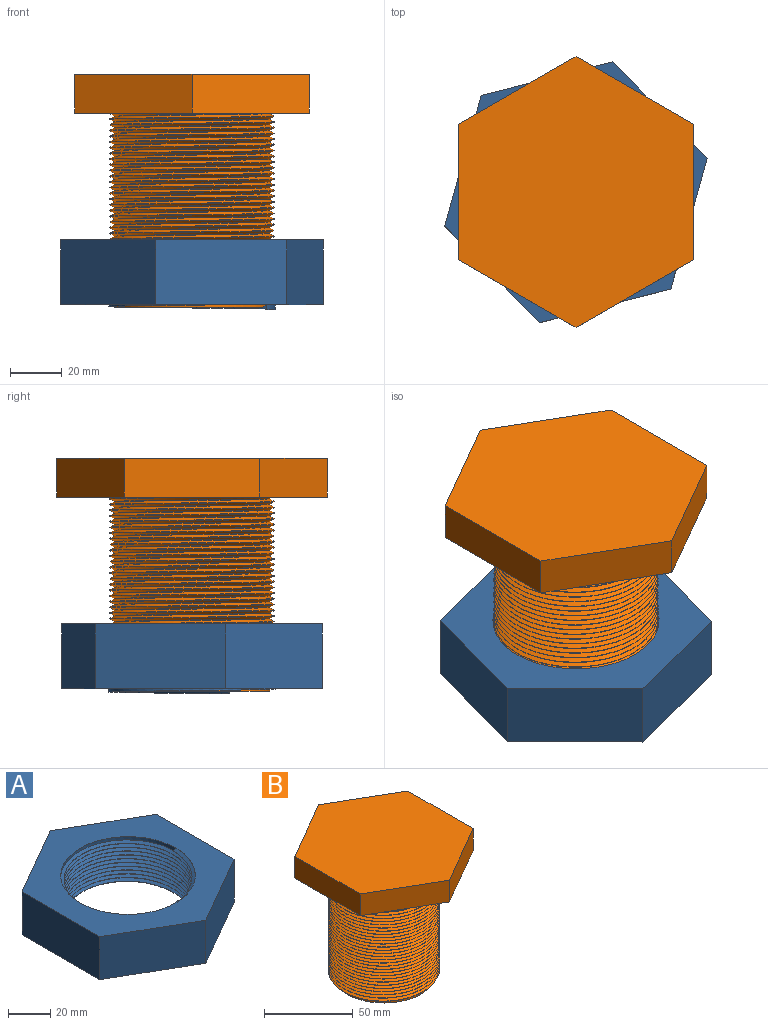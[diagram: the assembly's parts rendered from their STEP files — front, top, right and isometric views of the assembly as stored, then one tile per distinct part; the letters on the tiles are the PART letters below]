
ASSEMBLY  parts=2 mates=1
PART A: 16 faces, bbox 90.3x104.3x27.3 mm
  f0: cylinder r=32mm len=64mm, axis (0,0,-1), area 1153.5mm2, adj f1,f8,f9,f10,f12,f14
  f1: plane 104.31x90.34mm, normal (0,0,1), area 3849.1mm2, adj f0,f2,f3,f4,f5,f6,f7,f9
  f2: plane 52.15x25mm, normal (1,0,0), area 1303.8mm2, adj f1,f3,f7,f8
  f3: plane 45.16x26.08mm, normal (0.5,-0.87,0), area 1303.8mm2, adj f1,f2,f4,f8
  f4: plane 45.16x26.08mm, normal (-0.5,-0.87,0), area 1303.8mm2, adj f1,f3,f5,f8
  f5: plane 52.15x25mm, normal (-1,0,0), area 1303.8mm2, adj f1,f4,f6,f8
  f6: plane 45.16x26.08mm, normal (-0.5,0.87,0), area 1303.8mm2, adj f1,f5,f7,f8
  f7: plane 45.16x26.08mm, normal (0.5,0.87,0), area 1303.8mm2, adj f1,f2,f6,f8
  f8: plane 104.31x90.34mm, normal (0,0,-1), area 3841.2mm2, adj f0,f2,f3,f4,f5,f6,f7,f10
  f9: plane 1.97x1.6mm, normal (0,1,0), area 1.6mm2, adj f0,f1,f11,f12,f14,f15
  f10: plane 1.98x1.22mm, normal (-0.76,0.65,0), area 1.7mm2, adj f0,f8,f12,f13,f14,f15
  f11: cylinder r=32.05mm len=4.85mm, axis (0,0,-1), area 0.1mm2, adj f1,f9,f14
  f12: bspline ~74.01x64.09mm, area 4018.2mm2, adj f0,f8,f9,f10,f13,f15
  f13: cylinder r=32.05mm len=64.09mm, axis (0,0,-1), area 174.2mm2, adj f8,f10,f12
  f14: bspline ~74.01x64.09mm, area 3990.6mm2, adj f0,f1,f9,f10,f11,f15
  f15: cylinder r=30.45mm len=60.89mm, axis (0,0,-1), area 327.6mm2, adj f9,f10,f12,f14
PART B: 14 faces, bbox 90.3x104.3x89.8 mm
  f0: plane 45.16x26.08mm, normal (-0.5,0.87,0), area 782.3mm2, adj f1,f5,f6,f7
  f1: plane 52.15x15mm, normal (-1,0,0), area 782.3mm2, adj f0,f2,f6,f7
  f2: plane 45.16x26.08mm, normal (-0.5,-0.87,0), area 782.3mm2, adj f1,f3,f6,f7
  f3: plane 45.16x26.08mm, normal (0.5,-0.87,0), area 782.3mm2, adj f2,f4,f6,f7
  f4: plane 52.15x15mm, normal (1,0,0), area 782.3mm2, adj f3,f5,f6,f7
  f5: plane 45.16x26.08mm, normal (0.5,0.87,0), area 782.3mm2, adj f0,f4,f6,f7
  f6: plane 104.3x90.33mm, normal (0,0,1), area 7066.2mm2, adj f0,f1,f2,f3,f4,f5
  f7: plane 104.3x90.33mm, normal (0,0,-1), area 4088.4mm2, adj f0,f1,f2,f3,f4,f5,f8,f10
  f8: cylinder r=30mm len=74.8mm, axis (0,0,1), area 2474.2mm2, adj f7,f9,f10,f12,f13
  f9: plane 60x60mm, normal (0,0,-1), area 2827.4mm2, adj f8
  f10: bspline ~75.72x72.98mm, area 12076.3mm2, adj f7,f8,f11,f13
  f11: cylinder r=31.6mm len=73.88mm, axis (0,0,1), area 212.4mm2, adj f7,f10,f12,f13
  f12: bspline ~74.99x72.98mm, area 11926.3mm2, adj f7,f8,f11,f13
  f13: plane 2x1.6mm, normal (0,-1,0), area 1.7mm2, adj f8,f10,f11,f12
PLACE A rot(axis=(0,0,1),104.4deg) t=(-44.46,-33.39,19.32)mm
PLACE B t=(-44.46,-33.39,18.32)mm fixed
MATE cylindrical B.f8 <-> A.f0  axis (0,0,-1) through (-44.46,-33.39,-56.48)mm
